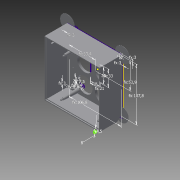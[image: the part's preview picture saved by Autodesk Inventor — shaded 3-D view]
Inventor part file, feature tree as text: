
AUTODESK INVENTOR PART (.ipt)
format: ipt  version: 2013 (Build 170138000, 138)  size: 416,768 bytes
history: native  units: mm
features: extrude x17, sketch x11, chamfer x6, draft x4, projected_geometry x4, other x2
ambient origin geometry x8: Origin, YZ Plane, XZ Plane, XY Plane, X Axis, Y Axis, Z Axis, Center Point
bodies: Solid3 (feature_tree), Solid4 (feature_tree)
feature tree (44):
  sketch  "Sketch1"  dims[d0=99.0mm d2=100.0mm]
  extrude  "Extrusion2"  Depth=100.0mm
  extrude  "Extrusion3"  Depth=31.5mm
  chamfer  "Chamfer1"  Distance=30.0mm
  chamfer  "Chamfer2"  Distance=13.5mm
  chamfer  "Chamfer3"  Distance=3.0mm
  extrude  "Extrusion4"  Depth=23.5mm
  extrude  "Extrusion5"  Depth=17.5mm
  draft  "FaceDraft1"
  draft  "FaceDraft2"
  draft  "FaceDraft3"
  draft  "FaceDraft4"
  extrude  "Extrusion6"  Depth=3.5mm
  extrude  "Extrusion7"  Depth=3.5mm
  other  "Lip1"
  chamfer  "Chamfer5"  Distance=3.0mm
  chamfer  "Chamfer6"  Distance=19.5mm
  chamfer  "Chamfer7"  Distance=50.0mm
  extrude  "Mouse Ears"  Depth=49.5mm
  sketch  "Sketch12"  dims[d8=43.0mm]
  extrude  "Extrusion9"  Depth=80.0mm
  extrude  "Extrusion10"  Depth=38.0mm
  extrude  "Extrusion11"  Depth=19.0mm
  extrude  "Extrusion12"  Depth=1.0mm
  extrude  "Extrusion13"  Depth=9.5mm
  other  "Lip2"
  sketch  "Sketch15"  dims[d11=19.0mm]
  extrude  "Extrusion14"  Depth=1.5mm
  extrude  "Extrusion15"  Depth=1.5mm
  extrude  "Extrusion16"  Depth=4.5mm TaperAngle=0.0deg
  sketch  "Sketch17"  dims[d13=33.0mm d14=30.0mm d15=13.5mm d16=3.0mm d17=23.5mm d18=17.5mm d19=3.5mm d20=3.5mm d21=3.0mm d22=19.5mm d23=50.0mm d24=49.5mm d27=80.0mm d30=38.0mm d31=19.0mm d32=1.0mm d33=9.5mm d34=1.5mm d35=1.5mm d67=4.5mm d68=0.0mm d69=3.0mm d70=0.0mm d71=1.5mm d72=2.0mm d73=45.0deg d74=1.5mm d75=2.0mm d76=45.0deg d77=1.5mm d78=2.0mm d79=45.0deg d80=3.9mm d81=3.9mm d82=3.9mm d83=3.9mm d84=3.0mm d85=3.0mm d86=3.0mm d87=3.0mm d88=45.3mm d89=0.0mm d115=4.5mm d116=31.8mm d117=0.0mm d118=0.523599mm d119=0.523599mm d120=0.523599mm d121=0.523599mm d122=2.8mm d126=2.8mm d127=2.8mm d128=2.8mm d129=4.0mm d130=0.0mm d131=4.9mm d132=10.5mm d133=11.2mm d134=0.0mm d135=4.0mm d136=0.0mm d137=2.0mm d138=1.5mm d139=0.0mm d140=0.0mm d141=0.0mm d142=0.0mm d147=7.0mm d148=2.0mm d149=45.0deg d151=3.0mm d152=2.0mm d153=45.0deg d154=3.0mm d155=2.0mm d156=45.0deg d157=30.0mm d158=30.0mm d159=30.0mm d160=30.0mm d161=0.45mm d162=0.0mm d163=107.8mm d164=106.8mm d165=107.8mm d167=106.8mm d168=53.4mm d169=53.9mm d170=3.0mm d171=3.0mm d172=3.0mm d173=3.0mm d174=18.0mm d175=30.0mm d176=5.0mm d177=0.0mm d178=21.0mm d179=33.0mm d180=11.0mm d181=0.0mm d182=3.0mm d183=0.0mm d184=3.0mm d185=0.0mm d186=16.0mm d187=0.0mm d188=2.0mm d189=1.5mm d190=0.0mm d191=0.0mm d192=0.0mm d193=0.0mm d194=12.0mm d195=12.0mm d196=24.0mm d197=17.5mm d198=0.0mm d199=6.0mm d200=8.4mm d201=7.5mm d202=7.5mm d203=9.4mm d204=17.5mm d205=0.0mm d206=30.0mm d207=30.0mm d208=30.0mm d209=30.0mm d210=0.45mm d211=0.0mm d212=8.0mm d213=4.5mm d214=8.0mm d215=0.0mm d216=16.0mm d217=0.0mm]
  extrude  "Extrusion17"  Depth=3.0mm TaperAngle=0.0deg
  extrude  "Extrusion18"  Depth=1.5mm TaperAngle=45.0deg
  sketch  "Sketch5"  dims[d3=31.5mm d4=31.5mm]
  projected_geometry  "Projected Loop1"
  sketch  "Sketch6"  dims[d5=31.5mm]
  projected_geometry  "Projected Loop2"
  projected_geometry  "Projected Loop3"
  sketch  "Sketch10"  dims[d6=31.5mm]
  projected_geometry  "Projected Loop4"
  sketch  "Sketch11"  dims[d7=33.0mm]
  sketch  "Sketch13"  dims[d9=43.0mm]
  sketch  "Sketch14"  dims[d10=30.0mm]
  sketch  "Sketch16"  dims[d12=19.0mm]
